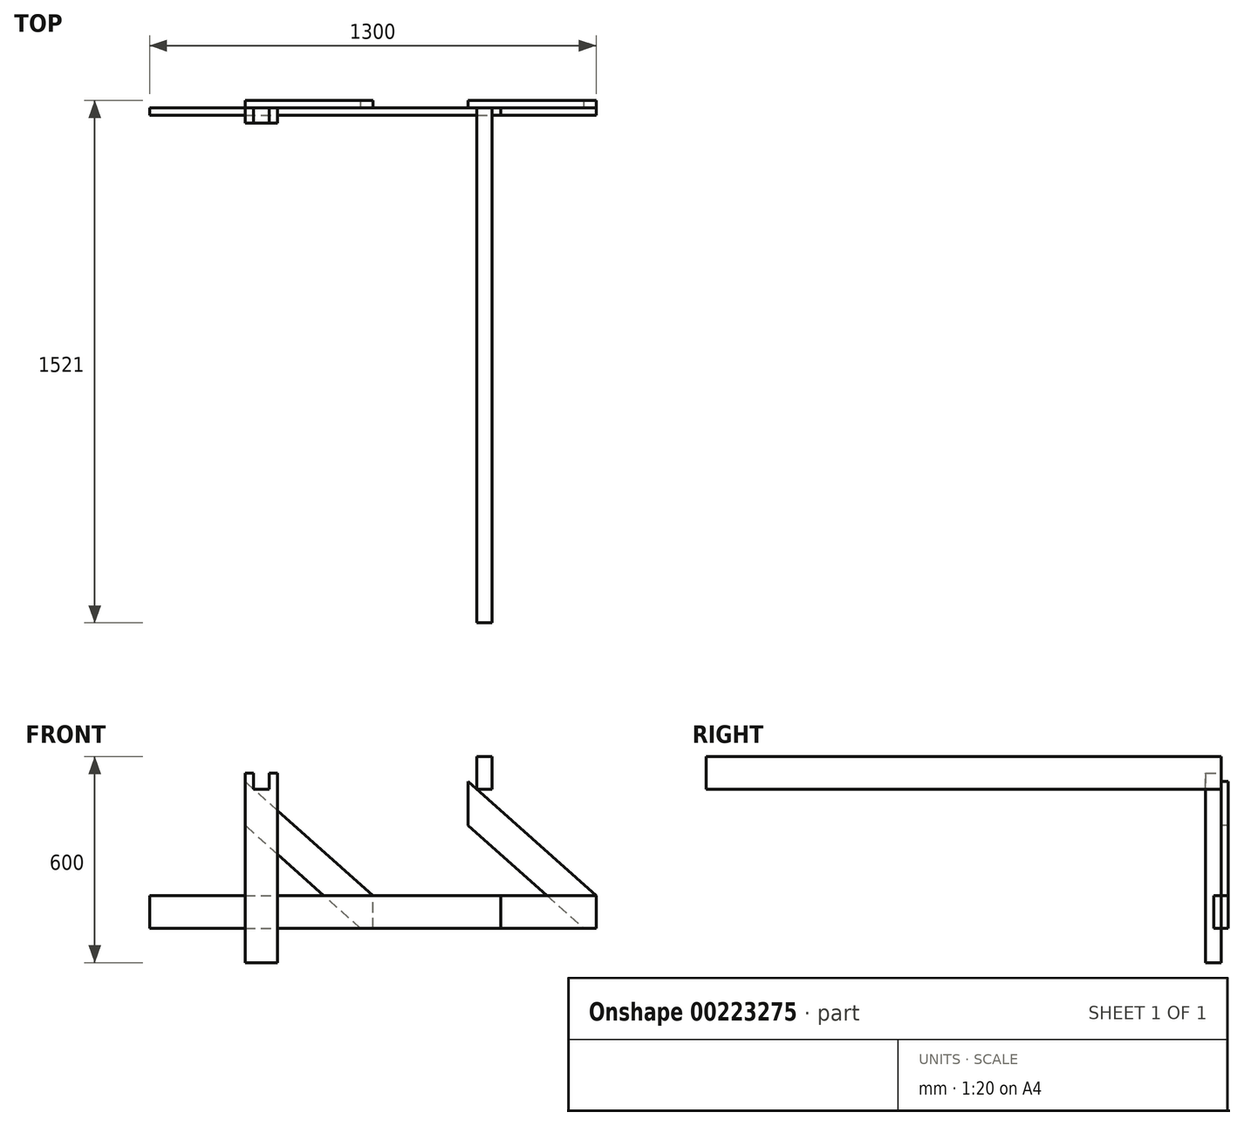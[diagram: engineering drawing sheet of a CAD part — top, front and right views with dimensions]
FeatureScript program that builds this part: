
annotation { "Feature Type Name" : "Feature", "Feature Type Description" : "" }
export const myFeature = defineFeature(function(context is Context, id is Id, definition is map)
    precondition{}
    {
        {
            var Q0;
            Q0=qCreatedBy(makeId("Front.planeOp"),FACE);
            var sketch = newSketch(context, id + "F0", { "sketchPlane" : qUnion([Q0])});
            skLineSegment(sketch, "E0", {"start": v(0, 600) * mm, "end": v(0, -600) * mm, "construction": true});
            skLineSegment(sketch, "E1.bottom", {"start": v(-302.5, 505) * mm, "end": v(-347.5, 505) * mm});
            skLineSegment(sketch, "E1.top", {"start": v(-302.5, 600) * mm, "end": v(-347.5, 600) * mm});
            skLineSegment(sketch, "E1.left", {"start": v(-302.5, 505) * mm, "end": v(-302.5, 600) * mm});
            skLineSegment(sketch, "E1.right", {"start": v(-347.5, 505) * mm, "end": v(-347.5, 600) * mm});
            skPoint(sketch, "E1.middle", {"position": v(-325, 552.5) * mm});
            skLineSegment(sketch, "E2.bottom", {"start": v(347.5, 505) * mm, "end": v(302.5, 505) * mm});
            skLineSegment(sketch, "E2.left", {"start": v(347.5, 505) * mm, "end": v(347.5, 600) * mm});
            skPoint(sketch, "E2.middle", {"position": v(325, 552.5) * mm});
            skPoint(sketch, "E3.orphan", {"position": v(302.5, 600) * mm});
            skLineSegment(sketch, "E4", {"start": v(347.5, 600) * mm, "end": v(302.5, 600) * mm});
            skLineSegment(sketch, "E5", {"start": v(302.5, 505) * mm, "end": v(302.5, 600) * mm});
            skLineSegment(sketch, "E6.bottom", {"start": v(-650, 195) * mm, "end": v(650, 195) * mm});
            skLineSegment(sketch, "E6.top", {"start": v(-650, 100) * mm, "end": v(650, 100) * mm});
            skLineSegment(sketch, "E6.left", {"start": v(-650, 195) * mm, "end": v(-650, 100) * mm});
            skLineSegment(sketch, "E6.right", {"start": v(650, 195) * mm, "end": v(650, 100) * mm});
            skPoint(sketch, "E6.middle", {"position": v(0, 147.5) * mm});
            skLineSegment(sketch, "E7", {"start": v(-372.5, 0) * mm, "end": v(-277.5, 0) * mm});
            skLineSegment(sketch, "E8", {"start": v(-277.5, 0) * mm, "end": v(-277.5, 552.5) * mm});
            skLineSegment(sketch, "E9", {"start": v(-277.5, 552.5) * mm, "end": v(-302.5, 552.5) * mm});
            skLineSegment(sketch, "E10", {"start": v(372.5, 0) * mm, "end": v(277.5, 0) * mm});
            skLineSegment(sketch, "E11", {"start": v(277.5, 0) * mm, "end": v(277.5, 527.3) * mm});
            skLineSegment(sketch, "E12", {"start": v(277.5, 552.5) * mm, "end": v(302.5, 552.5) * mm});
            skLineSegment(sketch, "E13", {"start": v(650, 195) * mm, "end": v(277.5, 527.3) * mm});
            skLineSegment(sketch, "E14", {"start": v(277.5, 400) * mm, "end": v(613.78, 100) * mm});
            skPoint(sketch, "E15", {"position": v(-325, 147.5) * mm});
            skLineSegment(sketch, "E16", {"start": v(-372.5, 100) * mm, "end": v(-277.5, 195) * mm, "construction": true});
            skLineSegment(sketch, "E17", {"start": v(-277.5, 100) * mm, "end": v(-372.5, 195) * mm, "construction": true});
            skLineSegment(sketch, "E18", {"start": v(277.5, 195) * mm, "end": v(372.5, 100) * mm, "construction": true});
            skLineSegment(sketch, "E19", {"start": v(372.5, 195) * mm, "end": v(277.5, 100) * mm, "construction": true});
            skPoint(sketch, "E20", {"position": v(325, 147.5) * mm});
            skLineSegment(sketch, "E21", {"start": v(277.5, 552.5) * mm, "end": v(277.5, 527.3) * mm});
            skLineSegment(sketch, "E22", {"start": v(-347.5, 552.5) * mm, "end": v(-372.5, 552.5) * mm});
            skLineSegment(sketch, "E23", {"start": v(-372.5, 552.5) * mm, "end": v(-372.5, 0) * mm});
            skLineSegment(sketch, "E24", {"start": v(347.5, 552.5) * mm, "end": v(372.5, 552.5) * mm});
            skLineSegment(sketch, "E25", {"start": v(372.5, 552.5) * mm, "end": v(372.5, 0) * mm});
            skLineSegment(sketch, "E26", {"start": v(0, 100) * mm, "end": v(0, 195) * mm});
            skLineSegment(sketch, "E27", {"start": v(0, 195) * mm, "end": v(-372.5, 527.3) * mm});
            skLineSegment(sketch, "E28", {"start": v(-36.22, 100) * mm, "end": v(-372.5, 400) * mm});
            skSolve(sketch);
        }
        {
            var Q0;
            {var subQ0=sQuery(id+"F0.wireOp",EDGE,"E23");var subQ1=sQuery(id+"F0.wireOp",EDGE,"E6.bottom");var subQ2=makeQuery(id+"F0.imprint","INTERSECT",VERTEX,{"derivedFrom":[subQ1,subQ0]});Q0=makeQuery(id+"F0.imprint","IMPRINT",FACE,{"disambiguationData":[TD([[makeQuery(id+"F0.imprint","IMPRINT",EDGE,{"disambiguationData":[TD([[subQ2,-1.0]])],"derivedFrom":subQ1}),-1.0]])]});}
            var Q1;
            {var subQ7=sQuery(id+"F0.wireOp",EDGE,"E1.bottom");Q1=makeQuery(id+"F0.imprint","IMPRINT",FACE,{"disambiguationData":[TD([[makeQuery(id+"F0.imprint","IMPRINT",EDGE,{"derivedFrom":subQ7}),1.0]])]});}
            var Q2;
            {var subQ5=sQuery(id+"F0.wireOp",EDGE,"E7");Q2=makeQuery(id+"F0.imprint","IMPRINT",FACE,{"disambiguationData":[TD([[makeQuery(id+"F0.imprint","IMPRINT",EDGE,{"derivedFrom":subQ5}),1.0]])]});}
            var Q3;
            {var subQ0=sQuery(id+"F0.wireOp",EDGE,"E23");var subQ1=sQuery(id+"F0.wireOp",EDGE,"E6.bottom");var subQ2=makeQuery(id+"F0.imprint","INTERSECT",VERTEX,{"derivedFrom":[subQ1,subQ0]});Q3=makeQuery(id+"F0.imprint","IMPRINT",FACE,{"disambiguationData":[TD([[makeQuery(id+"F0.imprint","IMPRINT",EDGE,{"disambiguationData":[TD([[subQ2,-1.0]])],"derivedFrom":subQ1}),1.0]])]});}
            var Q4;
            {var subQ0=sQuery(id+"F0.wireOp",EDGE,"E27");var subQ4=sQuery(id+"F0.wireOp",EDGE,"E8");var subQ5=makeQuery(id+"F0.imprint","INTERSECT",VERTEX,{"derivedFrom":[subQ4,subQ0]});Q4=makeQuery(id+"F0.imprint","IMPRINT",FACE,{"disambiguationData":[TD([[makeQuery(id+"F0.imprint","IMPRINT",EDGE,{"disambiguationData":[TD([[subQ5,1.0]])],"derivedFrom":subQ4}),1.0]])]});}
            var Q5;
            {var subQ3=sQuery(id+"F0.wireOp",EDGE,"E22");Q5=makeQuery(id+"F0.imprint","IMPRINT",FACE,{"disambiguationData":[TD([[makeQuery(id+"F0.imprint","IMPRINT",EDGE,{"derivedFrom":subQ3}),1.0]])]});}
            extrude(context, id + "F1", {"entities" : qUnion([Q0, Q1, Q2, Q3, Q4, Q5]), "depth" : 45 * mm});
        }
        {
            var Q0;
            Q0=makeQuery(id+"F1.opExtrude","SWEPT_FACE",FACE,{"disambiguationData":[OSD([sQuery(id+"F0.wireOp",EDGE,"E8")])]});
            var sketch = newSketch(context, id + "F2", { "sketchPlane" : qUnion([Q0])});
            skLineSegment(sketch, "E29.bottom", {"start": v(0, 195) * mm, "end": v(-21, 195) * mm});
            skLineSegment(sketch, "E29.top", {"start": v(0, 100) * mm, "end": v(-21, 100) * mm});
            skLineSegment(sketch, "E29.left", {"start": v(0, 195) * mm, "end": v(0, 100) * mm});
            skLineSegment(sketch, "E29.right", {"start": v(-21, 195) * mm, "end": v(-21, 100) * mm});
            skSolve(sketch);
        }
        {
            var Q0;
            Q0 = qSketchRegion(id + "F2", true);
            extrude(context, id + "F3", {"entities" : qUnion([Q0]), "operationType" : NewBodyOperationType.REMOVE, "endBound" : BoundingType.THROUGH_ALL, "oppositeDirection" : true, "depth" : 25 * mm});
        }
        {
            var Q0;
            {var subQ0=sQuery(id+"F0.wireOp",EDGE,"E6.left");Q0=makeQuery(id+"F0.imprint","IMPRINT",FACE,{"disambiguationData":[TD([[makeQuery(id+"F0.imprint","IMPRINT",EDGE,{"derivedFrom":subQ0}),1.0]])]});}
            var Q1;
            {var subQ0=sQuery(id+"F0.wireOp",EDGE,"E8");var subQ1=sQuery(id+"F0.wireOp",EDGE,"E6.bottom");var subQ2=makeQuery(id+"F0.imprint","INTERSECT",VERTEX,{"derivedFrom":[subQ1,subQ0]});Q1=makeQuery(id+"F0.imprint","IMPRINT",FACE,{"disambiguationData":[TD([[makeQuery(id+"F0.imprint","IMPRINT",EDGE,{"disambiguationData":[TD([[subQ2,-1.0]])],"derivedFrom":subQ1}),-1.0]])]});}
            var Q2;
            {var subQ0=sQuery(id+"F0.wireOp",EDGE,"E6.right");Q2=makeQuery(id+"F0.imprint","IMPRINT",FACE,{"disambiguationData":[TD([[makeQuery(id+"F0.imprint","IMPRINT",EDGE,{"derivedFrom":subQ0}),-1.0]])]});}
            var Q3;
            {var subQ0=sQuery(id+"F0.wireOp",EDGE,"E25");var subQ1=sQuery(id+"F0.wireOp",EDGE,"E6.bottom");var subQ2=makeQuery(id+"F0.imprint","INTERSECT",VERTEX,{"derivedFrom":[subQ1,subQ0]});Q3=makeQuery(id+"F0.imprint","IMPRINT",FACE,{"disambiguationData":[TD([[makeQuery(id+"F0.imprint","IMPRINT",EDGE,{"disambiguationData":[TD([[subQ2,-1.0]])],"derivedFrom":subQ1}),-1.0]])]});}
            var Q4;
            {var subQ0=sQuery(id+"F0.wireOp",EDGE,"E6.left");Q4=makeQuery(id+"F0.imprint","IMPRINT",FACE,{"disambiguationData":[TD([[makeQuery(id+"F0.imprint","IMPRINT",EDGE,{"derivedFrom":subQ0}),1.0]])]});}
            var Q5;
            {var subQ0=sQuery(id+"F0.wireOp",EDGE,"E8");var subQ1=sQuery(id+"F0.wireOp",EDGE,"E6.bottom");var subQ2=makeQuery(id+"F0.imprint","INTERSECT",VERTEX,{"derivedFrom":[subQ1,subQ0]});Q5=makeQuery(id+"F0.imprint","IMPRINT",FACE,{"disambiguationData":[TD([[makeQuery(id+"F0.imprint","IMPRINT",EDGE,{"disambiguationData":[TD([[subQ2,-1.0]])],"derivedFrom":subQ1}),-1.0]])]});}
            var Q6;
            {var subQ0=sQuery(id+"F0.wireOp",EDGE,"E6.right");Q6=makeQuery(id+"F0.imprint","IMPRINT",FACE,{"disambiguationData":[TD([[makeQuery(id+"F0.imprint","IMPRINT",EDGE,{"derivedFrom":subQ0}),-1.0]])]});}
            var Q7;
            {var subQ0=sQuery(id+"F0.wireOp",EDGE,"E25");var subQ1=sQuery(id+"F0.wireOp",EDGE,"E6.bottom");var subQ2=makeQuery(id+"F0.imprint","INTERSECT",VERTEX,{"derivedFrom":[subQ1,subQ0]});Q7=makeQuery(id+"F0.imprint","IMPRINT",FACE,{"disambiguationData":[TD([[makeQuery(id+"F0.imprint","IMPRINT",EDGE,{"disambiguationData":[TD([[subQ2,-1.0]])],"derivedFrom":subQ1}),-1.0]])]});}
            var Q8;
            {var subQ0=sQuery(id+"F0.wireOp",EDGE,"E8");var subQ1=sQuery(id+"F0.wireOp",EDGE,"E6.bottom");var subQ2=makeQuery(id+"F0.imprint","INTERSECT",VERTEX,{"derivedFrom":[subQ1,subQ0]});Q8=makeQuery(id+"F0.imprint","IMPRINT",FACE,{"disambiguationData":[TD([[makeQuery(id+"F0.imprint","IMPRINT",EDGE,{"disambiguationData":[TD([[subQ2,-1.0]])],"derivedFrom":subQ1}),-1.0]])]});}
            var Q9;
            {var subQ0=sQuery(id+"F0.wireOp",EDGE,"E6.left");Q9=makeQuery(id+"F0.imprint","IMPRINT",FACE,{"disambiguationData":[TD([[makeQuery(id+"F0.imprint","IMPRINT",EDGE,{"derivedFrom":subQ0}),1.0]])]});}
            var Q10;
            {var subQ0=sQuery(id+"F0.wireOp",EDGE,"E8");var subQ1=sQuery(id+"F0.wireOp",EDGE,"E6.bottom");var subQ2=makeQuery(id+"F0.imprint","INTERSECT",VERTEX,{"derivedFrom":[subQ1,subQ0]});Q10=makeQuery(id+"F0.imprint","IMPRINT",FACE,{"disambiguationData":[TD([[makeQuery(id+"F0.imprint","IMPRINT",EDGE,{"disambiguationData":[TD([[subQ2,-1.0]])],"derivedFrom":subQ1}),-1.0]])]});}
            var Q11;
            {var subQ0=sQuery(id+"F0.wireOp",EDGE,"E6.right");Q11=makeQuery(id+"F0.imprint","IMPRINT",FACE,{"disambiguationData":[TD([[makeQuery(id+"F0.imprint","IMPRINT",EDGE,{"derivedFrom":subQ0}),-1.0]])]});}
            var Q12;
            {var subQ0=sQuery(id+"F0.wireOp",EDGE,"E25");var subQ1=sQuery(id+"F0.wireOp",EDGE,"E6.bottom");var subQ2=makeQuery(id+"F0.imprint","INTERSECT",VERTEX,{"derivedFrom":[subQ1,subQ0]});Q12=makeQuery(id+"F0.imprint","IMPRINT",FACE,{"disambiguationData":[TD([[makeQuery(id+"F0.imprint","IMPRINT",EDGE,{"disambiguationData":[TD([[subQ2,-1.0]])],"derivedFrom":subQ1}),-1.0]])]});}
            var Q13;
            {var subQ0=sQuery(id+"F0.wireOp",EDGE,"E6.right");Q13=makeQuery(id+"F0.imprint","IMPRINT",FACE,{"disambiguationData":[TD([[makeQuery(id+"F0.imprint","IMPRINT",EDGE,{"derivedFrom":subQ0}),-1.0]])]});}
            var Q14;
            {var subQ0=sQuery(id+"F0.wireOp",EDGE,"E6.left");Q14=makeQuery(id+"F0.imprint","IMPRINT",FACE,{"disambiguationData":[TD([[makeQuery(id+"F0.imprint","IMPRINT",EDGE,{"derivedFrom":subQ0}),1.0]])]});}
            var Q15;
            {var subQ0=sQuery(id+"F0.wireOp",EDGE,"E23");var subQ1=sQuery(id+"F0.wireOp",EDGE,"E6.bottom");var subQ2=makeQuery(id+"F0.imprint","INTERSECT",VERTEX,{"derivedFrom":[subQ1,subQ0]});Q15=makeQuery(id+"F0.imprint","IMPRINT",FACE,{"disambiguationData":[TD([[makeQuery(id+"F0.imprint","IMPRINT",EDGE,{"disambiguationData":[TD([[subQ2,-1.0]])],"derivedFrom":subQ1}),-1.0]])]});}
            var Q16;
            {var subQ0=sQuery(id+"F0.wireOp",EDGE,"E11");var subQ1=sQuery(id+"F0.wireOp",EDGE,"E6.bottom");var subQ2=makeQuery(id+"F0.imprint","INTERSECT",VERTEX,{"derivedFrom":[subQ1,subQ0]});Q16=makeQuery(id+"F0.imprint","IMPRINT",FACE,{"disambiguationData":[TD([[makeQuery(id+"F0.imprint","IMPRINT",EDGE,{"disambiguationData":[TD([[subQ2,-1.0]])],"derivedFrom":subQ1}),-1.0]])]});}
            var Q17;
            {var subQ0=sQuery(id+"F0.wireOp",EDGE,"E26");Q17=makeQuery(id+"F0.imprint","IMPRINT",FACE,{"disambiguationData":[TD([[makeQuery(id+"F0.imprint","IMPRINT",EDGE,{"derivedFrom":subQ0}),-1.0]])]});}
            var Q18;
            {var subQ0=sQuery(id+"F0.wireOp",EDGE,"E26");Q18=makeQuery(id+"F0.imprint","IMPRINT",FACE,{"disambiguationData":[TD([[makeQuery(id+"F0.imprint","IMPRINT",EDGE,{"derivedFrom":subQ0}),1.0]])]});}
            extrude(context, id + "F4", {"entities" : qUnion([Q0, Q1, Q2, Q3, Q4, Q5, Q6, Q7, Q8, Q9, Q10, Q11, Q12, Q13, Q14, Q15, Q16, Q17, Q18]), "depth" : 21 * mm});
        }
        {
            var Q0;
            {var subQ1=sQuery(id+"F0.wireOp",EDGE,"E6.bottom");var subQ3=sQuery(id+"F0.wireOp",EDGE,"E14");var subQ4=makeQuery(id+"F0.imprint","INTERSECT",VERTEX,{"derivedFrom":[subQ1,subQ3]});Q0=makeQuery(id+"F0.imprint","IMPRINT",FACE,{"disambiguationData":[TD([[makeQuery(id+"F0.imprint","IMPRINT",EDGE,{"disambiguationData":[TD([[subQ4,1.0]])],"derivedFrom":subQ3}),1.0]])]});}
            var Q1;
            {var subQ0=sQuery(id+"F0.wireOp",EDGE,"E14");var subQ1=sQuery(id+"F0.wireOp",EDGE,"E11");var subQ2=makeQuery(id+"F0.imprint","INTERSECT",VERTEX,{"derivedFrom":[subQ1,subQ0]});Q1=makeQuery(id+"F0.imprint","IMPRINT",FACE,{"disambiguationData":[TD([[makeQuery(id+"F0.imprint","IMPRINT",EDGE,{"disambiguationData":[TD([[subQ2,-1.0]])],"derivedFrom":subQ0}),1.0]])]});}
            var Q2;
            {var subQ0=sQuery(id+"F0.wireOp",EDGE,"E6.right");Q2=makeQuery(id+"F0.imprint","IMPRINT",FACE,{"disambiguationData":[TD([[makeQuery(id+"F0.imprint","IMPRINT",EDGE,{"derivedFrom":subQ0}),-1.0]])]});}
            extrude(context, id + "F5", {"entities" : qUnion([Q0, Q1, Q2]), "oppositeDirection" : true, "depth" : 21 * mm});
        }
        {
            var Q0;
            {var subQ5=sQuery(id+"F0.wireOp",EDGE,"E2.left");Q0=makeQuery(id+"F0.imprint","IMPRINT",FACE,{"disambiguationData":[TD([[makeQuery(id+"F0.imprint","IMPRINT",EDGE,{"derivedFrom":subQ5}),1.0]])]});}
            extrude(context, id + "F6", {"entities" : qUnion([Q0]), "depth" : 1500 * mm});
        }
        {
            var Q0;
            {var subQ0=sQuery(id+"F0.wireOp",EDGE,"E8");var subQ1=sQuery(id+"F0.wireOp",EDGE,"E6.bottom");var subQ2=makeQuery(id+"F0.imprint","INTERSECT",VERTEX,{"derivedFrom":[subQ1,subQ0]});Q0=makeQuery(id+"F0.imprint","IMPRINT",FACE,{"disambiguationData":[TD([[makeQuery(id+"F0.imprint","IMPRINT",EDGE,{"disambiguationData":[TD([[subQ2,-1.0]])],"derivedFrom":subQ1}),-1.0]])]});}
            var Q1;
            {var subQ0=sQuery(id+"F0.wireOp",EDGE,"E11");var subQ1=sQuery(id+"F0.wireOp",EDGE,"E6.bottom");var subQ2=makeQuery(id+"F0.imprint","INTERSECT",VERTEX,{"derivedFrom":[subQ1,subQ0]});Q1=makeQuery(id+"F0.imprint","IMPRINT",FACE,{"disambiguationData":[TD([[makeQuery(id+"F0.imprint","IMPRINT",EDGE,{"disambiguationData":[TD([[subQ2,-1.0]])],"derivedFrom":subQ1}),-1.0]])]});}
            var Q2;
            {var subQ0=sQuery(id+"F0.wireOp",EDGE,"E23");var subQ1=sQuery(id+"F0.wireOp",EDGE,"E6.bottom");var subQ2=makeQuery(id+"F0.imprint","INTERSECT",VERTEX,{"derivedFrom":[subQ1,subQ0]});Q2=makeQuery(id+"F0.imprint","IMPRINT",FACE,{"disambiguationData":[TD([[makeQuery(id+"F0.imprint","IMPRINT",EDGE,{"disambiguationData":[TD([[subQ2,-1.0]])],"derivedFrom":subQ1}),-1.0]])]});}
            var Q3;
            {var subQ0=sQuery(id+"F0.wireOp",EDGE,"E26");Q3=makeQuery(id+"F0.imprint","IMPRINT",FACE,{"disambiguationData":[TD([[makeQuery(id+"F0.imprint","IMPRINT",EDGE,{"derivedFrom":subQ0}),1.0]])]});}
            var Q4;
            {var subQ0=sQuery(id+"F0.wireOp",EDGE,"E26");Q4=makeQuery(id+"F0.imprint","IMPRINT",FACE,{"disambiguationData":[TD([[makeQuery(id+"F0.imprint","IMPRINT",EDGE,{"derivedFrom":subQ0}),-1.0]])]});}
            extrude(context, id + "F7", {"entities" : qUnion([Q0, Q1, Q2, Q3, Q4]), "depth" : 21 * mm});
        }
        {
            var Q0;
            {var subQ0=sQuery(id+"F0.wireOp",EDGE,"E27");var subQ5=sQuery(id+"F0.wireOp",EDGE,"E8");var subQ6=makeQuery(id+"F0.imprint","INTERSECT",VERTEX,{"derivedFrom":[subQ5,subQ0]});Q0=makeQuery(id+"F0.imprint","IMPRINT",FACE,{"disambiguationData":[TD([[makeQuery(id+"F0.imprint","IMPRINT",EDGE,{"disambiguationData":[TD([[subQ6,1.0]])],"derivedFrom":subQ5}),-1.0]])]});}
            var Q1;
            {var subQ0=sQuery(id+"F0.wireOp",EDGE,"E27");var subQ4=sQuery(id+"F0.wireOp",EDGE,"E8");var subQ5=makeQuery(id+"F0.imprint","INTERSECT",VERTEX,{"derivedFrom":[subQ4,subQ0]});Q1=makeQuery(id+"F0.imprint","IMPRINT",FACE,{"disambiguationData":[TD([[makeQuery(id+"F0.imprint","IMPRINT",EDGE,{"disambiguationData":[TD([[subQ5,1.0]])],"derivedFrom":subQ4}),1.0]])]});}
            var Q2;
            {var subQ0=sQuery(id+"F0.wireOp",EDGE,"E26");Q2=makeQuery(id+"F0.imprint","IMPRINT",FACE,{"disambiguationData":[TD([[makeQuery(id+"F0.imprint","IMPRINT",EDGE,{"derivedFrom":subQ0}),1.0]])]});}
            extrude(context, id + "F8", {"entities" : qUnion([Q0, Q1, Q2]), "oppositeDirection" : true, "depth" : 21 * mm});
        }
    });
